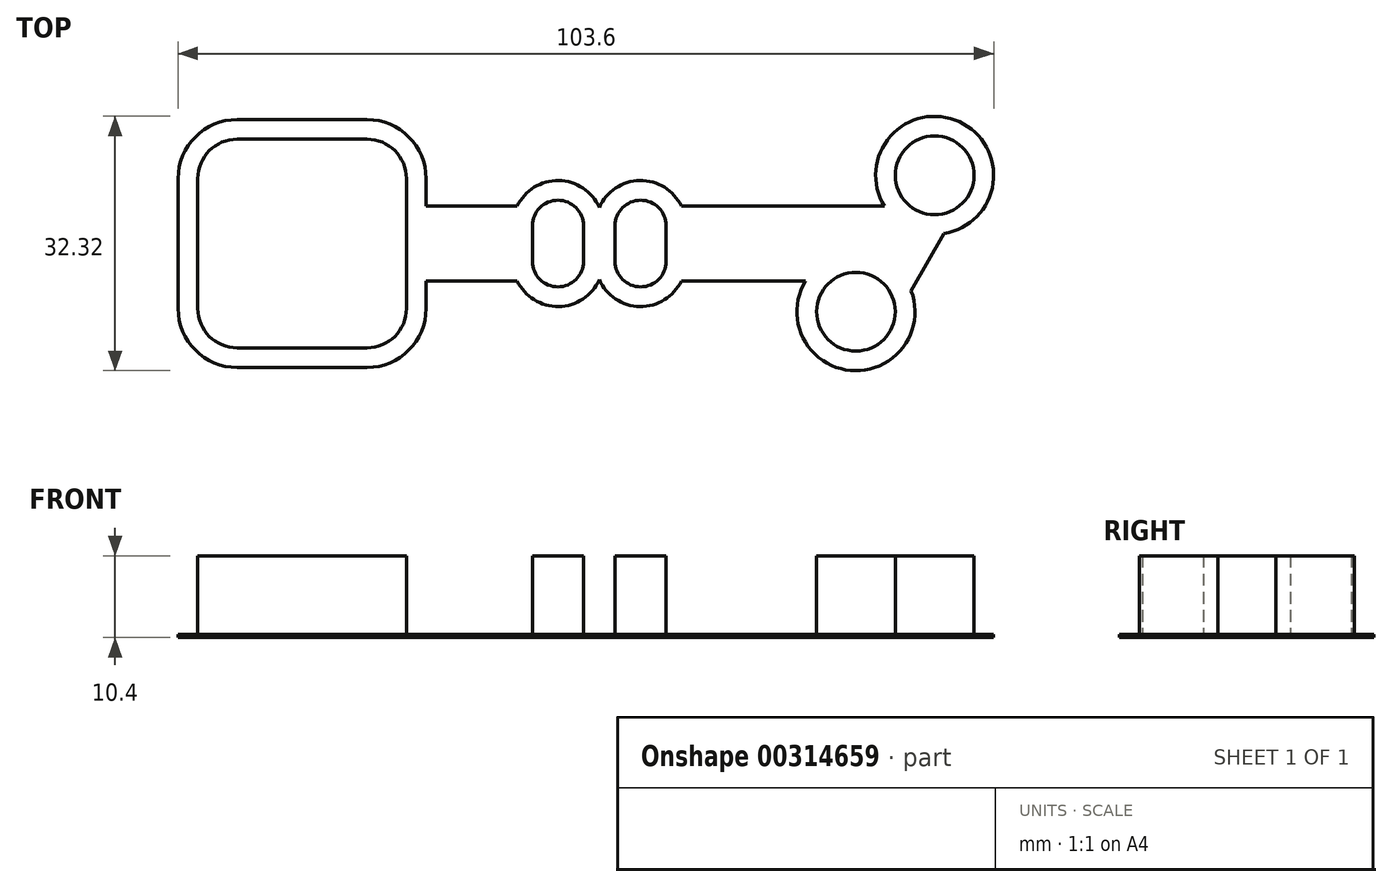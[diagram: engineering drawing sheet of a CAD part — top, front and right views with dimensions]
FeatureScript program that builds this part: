
annotation { "Feature Type Name" : "Feature", "Feature Type Description" : "" }
export const myFeature = defineFeature(function(context is Context, id is Id, definition is map)
    precondition{}
    {
        {
            var Q0;
            Q0=qCreatedBy(makeId("Top.planeOp"),FACE);
            var sketch = newSketch(context, id + "F0", { "sketchPlane" : qUnion([Q0])});
            skLineSegment(sketch, "E0.bottom", {"start": v(-8.25, 13.25) * mm, "end": v(8.25, 13.25) * mm});
            skLineSegment(sketch, "E0.top", {"start": v(-8.25, -13.25) * mm, "end": v(8.25, -13.25) * mm});
            skLineSegment(sketch, "E0.left", {"start": v(-13.25, 8.25) * mm, "end": v(-13.25, -8.25) * mm});
            skLineSegment(sketch, "E0.right", {"start": v(13.25, 8.25) * mm, "end": v(13.25, 2.25) * mm});
            skPoint(sketch, "E0.middle", {"position": v(0, 0) * mm});
            skPoint(sketch, "E1.visualSharp", {"position": v(-13.25, 13.25) * mm});
            skArc(sketch, "E1.filletArc", {"start": v(-8.25, 13.25) * mm, "mid": v(-11.79, 11.79) * mm, "end": v(-13.25, 8.25) * mm});
            skPoint(sketch, "E2.visualSharp", {"position": v(13.25, 13.25) * mm});
            skArc(sketch, "E2.filletArc", {"start": v(13.25, 8.25) * mm, "mid": v(11.79, 11.79) * mm, "end": v(8.25, 13.25) * mm});
            skPoint(sketch, "E3.visualSharp", {"position": v(13.25, -13.25) * mm});
            skArc(sketch, "E3.filletArc", {"start": v(8.25, -13.25) * mm, "mid": v(11.79, -11.79) * mm, "end": v(13.25, -8.25) * mm});
            skPoint(sketch, "E4.visualSharp", {"position": v(-13.25, -13.25) * mm});
            skArc(sketch, "E4.filletArc", {"start": v(-13.25, -8.25) * mm, "mid": v(-11.79, -11.79) * mm, "end": v(-8.25, -13.25) * mm});
            skCircle(sketch, "E5", {"center": v(0, 0) * mm, "radius": 4.5 * mm});
            skLineSegment(sketch, "E6", {"start": v(-4.5, 13.25) * mm, "end": v(-4.5, -13.25) * mm});
            skLineSegment(sketch, "E7", {"start": v(4.5, 13.25) * mm, "end": v(4.5, -13.25) * mm});
            skLineSegment(sketch, "E8", {"start": v(-13.25, 4.5) * mm, "end": v(13.25, 4.5) * mm});
            skLineSegment(sketch, "E9", {"start": v(-13.25, -4.5) * mm, "end": v(13.25, -4.5) * mm});
            skLineSegment(sketch, "E10", {"start": v(-29.26, 0) * mm, "end": v(84.97, 0) * mm, "construction": true});
            skPoint(sketch, "E10.startSnap0", {"position": v(-4.5, 0) * mm});
            skPoint(sketch, "E10.endSnap0", {"position": v(13.25, 0) * mm});
            skLineSegment(sketch, "E11", {"start": v(13.25, 2.25) * mm, "end": v(29.25, 2.25) * mm});
            skLineSegment(sketch, "E12.bottom", {"start": v(29.25, 2.25) * mm, "end": v(35.75, 2.25) * mm});
            skLineSegment(sketch, "E12.top", {"start": v(29.25, -2.25) * mm, "end": v(35.75, -2.25) * mm});
            skLineSegment(sketch, "E12.left", {"start": v(29.25, 2.25) * mm, "end": v(29.25, -2.25) * mm});
            skLineSegment(sketch, "E12.right", {"start": v(35.75, 2.25) * mm, "end": v(35.75, -2.25) * mm});
            skLineSegment(sketch, "E13", {"start": v(37.75, 11.92) * mm, "end": v(37.75, -12.1) * mm, "construction": true});
            skLineSegment(sketch, "E14.MirrorCS", {"start": v(13.25, -2.25) * mm, "end": v(29.25, -2.25) * mm});
            skLineSegment(sketch, "E15.MirrorCS", {"start": v(46.25, 2.25) * mm, "end": v(39.75, 2.25) * mm});
            skLineSegment(sketch, "E16.MirrorCS", {"start": v(39.75, 2.25) * mm, "end": v(39.75, -2.25) * mm});
            skLineSegment(sketch, "E17.MirrorCS", {"start": v(46.25, -2.25) * mm, "end": v(39.75, -2.25) * mm});
            skLineSegment(sketch, "E18.MirrorCS", {"start": v(46.25, 2.25) * mm, "end": v(46.25, -2.25) * mm});
            skLineSegment(sketch, "E19", {"start": v(35.75, -2.25) * mm, "end": v(39.75, -2.25) * mm});
            skLineSegment(sketch, "E20", {"start": v(35.75, 2.25) * mm, "end": v(39.75, 2.25) * mm});
            skArc(sketch, "E21", {"start": v(29.25, 2.25) * mm, "mid": v(32.5, 5.5) * mm, "end": v(35.75, 2.25) * mm});
            skArc(sketch, "E22", {"start": v(29.25, -2.25) * mm, "mid": v(32.5, -5.5) * mm, "end": v(35.75, -2.25) * mm});
            skArc(sketch, "E23.MirrorCS", {"start": v(46.25, 2.25) * mm, "mid": v(43, 5.5) * mm, "end": v(39.75, 2.25) * mm});
            skArc(sketch, "E24.MirrorCS", {"start": v(46.25, -2.25) * mm, "mid": v(43, -5.5) * mm, "end": v(39.75, -2.25) * mm});
            skLineSegment(sketch, "E25", {"start": v(46.25, 2.25) * mm, "end": v(74.05, 2.25) * mm});
            skLineSegment(sketch, "E26", {"start": v(70.35, -8.66) * mm, "end": v(80.35, 8.66) * mm, "construction": true});
            skPoint(sketch, "E27", {"position": v(75.35, 0) * mm});
            skLineSegment(sketch, "E28", {"start": v(76.17, 5.92) * mm, "end": v(74.05, 2.25) * mm});
            skLineSegment(sketch, "E29.MirrorCS", {"start": v(80.06, 3.67) * mm, "end": v(80.06, 3.67) * mm});
            skPoint(sketch, "E30", {"position": v(72.75, 0) * mm});
            skLineSegment(sketch, "E31.MirrorCS", {"start": v(46.25, -2.25) * mm, "end": v(71.45, -2.25) * mm});
            skPoint(sketch, "E32.orphan", {"position": v(72.75, -2.25) * mm});
            skPoint(sketch, "E33.orphan", {"position": v(72.75, 2.25) * mm});
            skLineSegment(sketch, "E34", {"start": v(13.25, 2.25) * mm, "end": v(13.25, 2.25) * mm});
            skArc(sketch, "E35", {"start": v(74.53, -5.92) * mm, "mid": v(72.85, -4.33) * mm, "end": v(70.63, -3.67) * mm});
            skArc(sketch, "E36", {"start": v(70.63, -3.67) * mm, "mid": v(67.85, -13) * mm, "end": v(74.53, -5.92) * mm});
            skLineSegment(sketch, "E37", {"start": v(80.06, 3.67) * mm, "end": v(74.53, -5.92) * mm});
            skArc(sketch, "E38", {"start": v(76.17, 5.92) * mm, "mid": v(77.85, 4.33) * mm, "end": v(80.06, 3.67) * mm});
            skArc(sketch, "E39", {"start": v(80.06, 3.67) * mm, "mid": v(82.85, 13) * mm, "end": v(76.17, 5.92) * mm});
            skLineSegment(sketch, "E40", {"start": v(13.25, -2.25) * mm, "end": v(13.25, -2.25) * mm});
            skLineSegment(sketch, "E41", {"start": v(13.25, -2.25) * mm, "end": v(13.25, -8.25) * mm});
            skLineSegment(sketch, "E42", {"start": v(13.25, 2.25) * mm, "end": v(13.25, -2.25) * mm});
            skLineSegment(sketch, "E43", {"start": v(71.45, -2.25) * mm, "end": v(70.63, -3.67) * mm});
            skLineSegment(sketch, "E44", {"start": v(74.05, 2.25) * mm, "end": v(71.45, -2.25) * mm});
            skLineSegment(sketch, "E45.0", {"start": v(81.56, 1.26) * mm, "end": v(77.36, -6) * mm});
            skArc(sketch, "E45.1", {"start": v(63.95, -4.75) * mm, "mid": v(69.65, -16.13) * mm, "end": v(77.36, -6) * mm});
            skLineSegment(sketch, "E45.2", {"start": v(48.18, -4.75) * mm, "end": v(63.95, -4.75) * mm});
            skArc(sketch, "E45.3", {"start": v(48.18, -4.75) * mm, "mid": v(42.91, -8) * mm, "end": v(37.75, -4.6) * mm});
            skArc(sketch, "E45.4", {"start": v(27.32, -4.75) * mm, "mid": v(32.59, -8) * mm, "end": v(37.75, -4.6) * mm});
            skArc(sketch, "E45.5", {"start": v(81.56, 1.26) * mm, "mid": v(83.47, 15.48) * mm, "end": v(73.95, 4.75) * mm});
            skLineSegment(sketch, "E45.6", {"start": v(15.75, -4.75) * mm, "end": v(27.32, -4.75) * mm});
            skLineSegment(sketch, "E45.7", {"start": v(15.75, -4.75) * mm, "end": v(15.75, -8.25) * mm});
            skArc(sketch, "E45.8", {"start": v(8.25, -15.75) * mm, "mid": v(13.55, -13.55) * mm, "end": v(15.75, -8.25) * mm});
            skLineSegment(sketch, "E45.9", {"start": v(-8.25, -15.75) * mm, "end": v(8.25, -15.75) * mm});
            skLineSegment(sketch, "E45.10", {"start": v(15.75, 4.75) * mm, "end": v(27.32, 4.75) * mm});
            skArc(sketch, "E45.11", {"start": v(27.32, 4.75) * mm, "mid": v(32.59, 8) * mm, "end": v(37.75, 4.6) * mm});
            skArc(sketch, "E45.12", {"start": v(48.18, 4.75) * mm, "mid": v(42.91, 8) * mm, "end": v(37.75, 4.6) * mm});
            skLineSegment(sketch, "E45.13", {"start": v(48.18, 4.75) * mm, "end": v(73.95, 4.75) * mm});
            skLineSegment(sketch, "E45.14", {"start": v(15.75, 8.25) * mm, "end": v(15.75, 4.75) * mm});
            skArc(sketch, "E45.15", {"start": v(15.75, 8.25) * mm, "mid": v(13.55, 13.55) * mm, "end": v(8.25, 15.75) * mm});
            skLineSegment(sketch, "E45.16", {"start": v(-8.25, 15.75) * mm, "end": v(8.25, 15.75) * mm});
            skArc(sketch, "E45.17", {"start": v(-8.25, 15.75) * mm, "mid": v(-13.55, 13.55) * mm, "end": v(-15.75, 8.25) * mm});
            skLineSegment(sketch, "E45.18", {"start": v(-15.75, 8.25) * mm, "end": v(-15.75, -8.25) * mm});
            skArc(sketch, "E45.19", {"start": v(-15.75, -8.25) * mm, "mid": v(-13.55, -13.55) * mm, "end": v(-8.25, -15.75) * mm});
            skSolve(sketch);
        }
        {
            var Q0;
            Q0=makeQuery(id+"F0.imprint","IMPRINT",FACE,{"disambiguationData":[TD([[makeQuery(id+"F0.imprint","IMPRINT",EDGE,{"derivedFrom":sQuery(id+"F0.wireOp",EDGE,"E12.right")}),1.0]])]});
            var Q1;
            {var subQ0=sQuery(id+"F0.wireOp",EDGE,"E7");var subQ1=sQuery(id+"F0.wireOp",EDGE,"E5");var subQ2=makeQuery(id+"F0.imprint","INTERSECT",VERTEX,{"derivedFrom":[subQ1,subQ0]});Q1=makeQuery(id+"F0.imprint","IMPRINT",FACE,{"disambiguationData":[TD([[makeQuery(id+"F0.imprint","IMPRINT",EDGE,{"disambiguationData":[TD([[subQ2,1.0]])],"derivedFrom":subQ1}),-1.0]])]});}
            var Q2;
            {var subQ5=sQuery(id+"F0.wireOp",EDGE,"E4.filletArc");Q2=makeQuery(id+"F0.imprint","IMPRINT",FACE,{"disambiguationData":[TD([[makeQuery(id+"F0.imprint","IMPRINT",EDGE,{"derivedFrom":subQ5}),1.0]])]});}
            var Q3;
            {var subQ1=sQuery(id+"F0.wireOp",EDGE,"E0.top");var subQ5=sQuery(id+"F0.wireOp",EDGE,"E6");var subQ6=makeQuery(id+"F0.imprint","INTERSECT",VERTEX,{"derivedFrom":[subQ1,subQ5]});Q3=makeQuery(id+"F0.imprint","IMPRINT",FACE,{"disambiguationData":[TD([[makeQuery(id+"F0.imprint","IMPRINT",EDGE,{"disambiguationData":[TD([[subQ6,-1.0]])],"derivedFrom":subQ1}),1.0]])]});}
            var Q4;
            Q4=makeQuery(id+"F0.imprint","IMPRINT",FACE,{"disambiguationData":[TD([[makeQuery(id+"F0.imprint","IMPRINT",EDGE,{"derivedFrom":sQuery(id+"F0.wireOp",EDGE,"E11")}),-1.0]])]});
            var Q5;
            Q5=makeQuery(id+"F0.imprint","IMPRINT",FACE,{"disambiguationData":[TD([[makeQuery(id+"F0.imprint","IMPRINT",EDGE,{"derivedFrom":sQuery(id+"F0.wireOp",EDGE,"E18.MirrorCS")}),1.0]])]});
            var Q6;
            Q6=makeQuery(id+"F0.imprint","IMPRINT",FACE,{"disambiguationData":[TD([[makeQuery(id+"F0.imprint","IMPRINT",EDGE,{"derivedFrom":sQuery(id+"F0.wireOp",EDGE,"E12.bottom")}),-1.0]])]});
            var Q7;
            Q7=makeQuery(id+"F0.imprint","IMPRINT",FACE,{"disambiguationData":[TD([[makeQuery(id+"F0.imprint","IMPRINT",EDGE,{"derivedFrom":sQuery(id+"F0.wireOp",EDGE,"E35")}),1.0]])]});
            var Q8;
            {var subQ8=sQuery(id+"F0.wireOp",EDGE,"E42");Q8=makeQuery(id+"F0.imprint","IMPRINT",FACE,{"disambiguationData":[TD([[makeQuery(id+"F0.imprint","IMPRINT",EDGE,{"derivedFrom":subQ8}),-1.0]])]});}
            var Q9;
            {var subQ4=sQuery(id+"F0.wireOp",EDGE,"E8");var subQ6=sQuery(id+"F0.wireOp",EDGE,"E0.left");var subQ8=makeQuery(id+"F0.imprint","INTERSECT",VERTEX,{"derivedFrom":[subQ6,subQ4]});Q9=makeQuery(id+"F0.imprint","IMPRINT",FACE,{"disambiguationData":[TD([[makeQuery(id+"F0.imprint","IMPRINT",EDGE,{"disambiguationData":[TD([[subQ8,-1.0]])],"derivedFrom":subQ6}),1.0]])]});}
            var Q10;
            {var subQ0=sQuery(id+"F0.wireOp",EDGE,"E5");var subQ1=makeQuery(id+"F0.imprint","INTERSECT",VERTEX,{"derivedFrom":[subQ0,sQuery(id+"F0.wireOp",EDGE,"E8")]});Q10=makeQuery(id+"F0.imprint","IMPRINT",FACE,{"disambiguationData":[TD([[makeQuery(id+"F0.imprint","IMPRINT",EDGE,{"disambiguationData":[TD([[subQ1,1.0]])],"derivedFrom":subQ0}),1.0]])]});}
            var Q11;
            {var subQ9=sQuery(id+"F0.wireOp",EDGE,"E1.filletArc");Q11=makeQuery(id+"F0.imprint","IMPRINT",FACE,{"disambiguationData":[TD([[makeQuery(id+"F0.imprint","IMPRINT",EDGE,{"derivedFrom":subQ9}),-1.0]])]});}
            var Q12;
            Q12=makeQuery(id+"F0.imprint","IMPRINT",FACE,{"disambiguationData":[TD([[makeQuery(id+"F0.imprint","IMPRINT",EDGE,{"derivedFrom":sQuery(id+"F0.wireOp",EDGE,"E38")}),1.0]])]});
            var Q13;
            {var subQ5=sQuery(id+"F0.wireOp",EDGE,"E2.filletArc");Q13=makeQuery(id+"F0.imprint","IMPRINT",FACE,{"disambiguationData":[TD([[makeQuery(id+"F0.imprint","IMPRINT",EDGE,{"derivedFrom":subQ5}),1.0]])]});}
            var Q14;
            {var subQ5=sQuery(id+"F0.wireOp",EDGE,"E1.filletArc");Q14=makeQuery(id+"F0.imprint","IMPRINT",FACE,{"disambiguationData":[TD([[makeQuery(id+"F0.imprint","IMPRINT",EDGE,{"derivedFrom":subQ5}),1.0]])]});}
            var Q15;
            {var subQ0=sQuery(id+"F0.wireOp",EDGE,"E8");var subQ1=sQuery(id+"F0.wireOp",EDGE,"E5");var subQ2=makeQuery(id+"F0.imprint","INTERSECT",VERTEX,{"derivedFrom":[subQ1,subQ0]});Q15=makeQuery(id+"F0.imprint","IMPRINT",FACE,{"disambiguationData":[TD([[makeQuery(id+"F0.imprint","IMPRINT",EDGE,{"disambiguationData":[TD([[subQ2,1.0]])],"derivedFrom":subQ1}),-1.0]])]});}
            var Q16;
            {var subQ0=sQuery(id+"F0.wireOp",EDGE,"E6");var subQ1=sQuery(id+"F0.wireOp",EDGE,"E5");var subQ2=makeQuery(id+"F0.imprint","INTERSECT",VERTEX,{"derivedFrom":[subQ1,subQ0]});Q16=makeQuery(id+"F0.imprint","IMPRINT",FACE,{"disambiguationData":[TD([[makeQuery(id+"F0.imprint","IMPRINT",EDGE,{"disambiguationData":[TD([[subQ2,-1.0]])],"derivedFrom":subQ1}),-1.0]])]});}
            var Q17;
            {var subQ0=sQuery(id+"F0.wireOp",EDGE,"E8");var subQ1=sQuery(id+"F0.wireOp",EDGE,"E5");var subQ2=makeQuery(id+"F0.imprint","INTERSECT",VERTEX,{"derivedFrom":[subQ1,subQ0]});Q17=makeQuery(id+"F0.imprint","IMPRINT",FACE,{"disambiguationData":[TD([[makeQuery(id+"F0.imprint","IMPRINT",EDGE,{"disambiguationData":[TD([[subQ2,-1.0]])],"derivedFrom":subQ1}),-1.0]])]});}
            var Q18;
            {var subQ7=sQuery(id+"F0.wireOp",EDGE,"E3.filletArc");Q18=makeQuery(id+"F0.imprint","IMPRINT",FACE,{"disambiguationData":[TD([[makeQuery(id+"F0.imprint","IMPRINT",EDGE,{"derivedFrom":subQ7}),1.0]])]});}
            var Q19;
            Q19=makeQuery(id+"F0.imprint","IMPRINT",FACE,{"disambiguationData":[TD([[makeQuery(id+"F0.imprint","IMPRINT",EDGE,{"derivedFrom":sQuery(id+"F0.wireOp",EDGE,"E17.MirrorCS")}),1.0]])]});
            var Q20;
            Q20=makeQuery(id+"F0.imprint","IMPRINT",FACE,{"disambiguationData":[TD([[makeQuery(id+"F0.imprint","IMPRINT",EDGE,{"derivedFrom":sQuery(id+"F0.wireOp",EDGE,"E15.MirrorCS")}),-1.0]])]});
            var Q21;
            Q21=makeQuery(id+"F0.imprint","IMPRINT",FACE,{"disambiguationData":[TD([[makeQuery(id+"F0.imprint","IMPRINT",EDGE,{"derivedFrom":sQuery(id+"F0.wireOp",EDGE,"E12.top")}),-1.0]])]});
            var Q22;
            Q22=makeQuery(id+"F0.imprint","IMPRINT",FACE,{"disambiguationData":[TD([[makeQuery(id+"F0.imprint","IMPRINT",EDGE,{"derivedFrom":sQuery(id+"F0.wireOp",EDGE,"E12.bottom")}),1.0]])]});
            var Q23;
            {var subQ2=sQuery(id+"F0.wireOp",EDGE,"E6");var subQ5=sQuery(id+"F0.wireOp",EDGE,"E0.bottom");var subQ8=makeQuery(id+"F0.imprint","INTERSECT",VERTEX,{"derivedFrom":[subQ5,subQ2]});Q23=makeQuery(id+"F0.imprint","IMPRINT",FACE,{"disambiguationData":[TD([[makeQuery(id+"F0.imprint","IMPRINT",EDGE,{"disambiguationData":[TD([[subQ8,-1.0]])],"derivedFrom":subQ5}),-1.0]])]});}
            var Q24;
            Q24=makeQuery(id+"F0.imprint","IMPRINT",FACE,{"disambiguationData":[TD([[makeQuery(id+"F0.imprint","IMPRINT",EDGE,{"derivedFrom":sQuery(id+"F0.wireOp",EDGE,"E28")}),1.0]])]});
            var Q25;
            Q25=makeQuery(id+"F0.imprint","IMPRINT",FACE,{"disambiguationData":[TD([[makeQuery(id+"F0.imprint","IMPRINT",EDGE,{"derivedFrom":sQuery(id+"F0.wireOp",EDGE,"E15.MirrorCS")}),1.0]])]});
            extrude(context, id + "F1", {"entities" : qUnion([Q0, Q1, Q2, Q3, Q4, Q5, Q6, Q7, Q8, Q9, Q10, Q11, Q12, Q13, Q14, Q15, Q16, Q17, Q18, Q19, Q20, Q21, Q22, Q23, Q24, Q25]), "depth" : 0.4 * mm});
        }
        {
            var Q0;
            Q0=makeQuery(id+"F1.opExtrude","CAP_FACE",FACE,{"disambiguationData":[OSD([sQuery(id+"F0.wireOp",EDGE,"E45.0"),sQuery(id+"F0.wireOp",EDGE,"E45.1"),sQuery(id+"F0.wireOp",EDGE,"E45.2"),sQuery(id+"F0.wireOp",EDGE,"E45.3"),sQuery(id+"F0.wireOp",EDGE,"E45.4"),sQuery(id+"F0.wireOp",EDGE,"E45.5"),sQuery(id+"F0.wireOp",EDGE,"E45.6"),sQuery(id+"F0.wireOp",EDGE,"E45.7"),sQuery(id+"F0.wireOp",EDGE,"E45.8"),sQuery(id+"F0.wireOp",EDGE,"E45.9"),sQuery(id+"F0.wireOp",EDGE,"E45.10"),sQuery(id+"F0.wireOp",EDGE,"E45.11"),sQuery(id+"F0.wireOp",EDGE,"E45.12"),sQuery(id+"F0.wireOp",EDGE,"E45.13"),sQuery(id+"F0.wireOp",EDGE,"E45.14"),sQuery(id+"F0.wireOp",EDGE,"E45.15"),sQuery(id+"F0.wireOp",EDGE,"E45.16"),sQuery(id+"F0.wireOp",EDGE,"E45.17"),sQuery(id+"F0.wireOp",EDGE,"E45.18"),sQuery(id+"F0.wireOp",EDGE,"E45.19")])],"isStart":false});
            var sketch = newSketch(context, id + "F2", { "sketchPlane" : qUnion([Q0])});
            skLineSegment(sketch, "E46.0.0", {"start": v(8.25, 15.75) * mm, "end": v(-8.25, 15.75) * mm});
            skArc(sketch, "E46.0.1", {"start": v(-8.25, 15.75) * mm, "mid": v(-13.55, 13.55) * mm, "end": v(-15.75, 8.25) * mm});
            skLineSegment(sketch, "E46.0.2", {"start": v(-15.75, 8.25) * mm, "end": v(-15.75, -8.25) * mm});
            skArc(sketch, "E46.0.3", {"start": v(-15.75, -8.25) * mm, "mid": v(-13.55, -13.55) * mm, "end": v(-8.25, -15.75) * mm});
            skLineSegment(sketch, "E46.0.4", {"start": v(-8.25, -15.75) * mm, "end": v(8.25, -15.75) * mm});
            skArc(sketch, "E46.0.5", {"start": v(8.25, -15.75) * mm, "mid": v(13.55, -13.55) * mm, "end": v(15.75, -8.25) * mm});
            skLineSegment(sketch, "E46.0.6", {"start": v(15.75, -8.25) * mm, "end": v(15.75, -4.75) * mm});
            skLineSegment(sketch, "E46.0.7", {"start": v(15.75, -4.75) * mm, "end": v(27.32, -4.75) * mm});
            skArc(sketch, "E46.0.8", {"start": v(27.32, -4.75) * mm, "mid": v(32.59, -8) * mm, "end": v(37.75, -4.6) * mm});
            skArc(sketch, "E46.0.9", {"start": v(37.75, -4.6) * mm, "mid": v(42.91, -8) * mm, "end": v(48.18, -4.75) * mm});
            skLineSegment(sketch, "E46.0.10", {"start": v(48.18, -4.75) * mm, "end": v(63.95, -4.75) * mm});
            skArc(sketch, "E46.0.11", {"start": v(63.95, -4.75) * mm, "mid": v(69.65, -16.13) * mm, "end": v(77.36, -6) * mm});
            skLineSegment(sketch, "E46.0.12", {"start": v(77.36, -6) * mm, "end": v(81.56, 1.26) * mm});
            skArc(sketch, "E46.0.13", {"start": v(81.56, 1.26) * mm, "mid": v(83.47, 15.48) * mm, "end": v(73.95, 4.75) * mm});
            skLineSegment(sketch, "E46.0.14", {"start": v(73.95, 4.75) * mm, "end": v(48.18, 4.75) * mm});
            skArc(sketch, "E46.0.15", {"start": v(48.18, 4.75) * mm, "mid": v(42.91, 8) * mm, "end": v(37.75, 4.6) * mm});
            skArc(sketch, "E46.0.16", {"start": v(37.75, 4.6) * mm, "mid": v(32.59, 8) * mm, "end": v(27.32, 4.75) * mm});
            skLineSegment(sketch, "E46.0.17", {"start": v(27.32, 4.75) * mm, "end": v(15.75, 4.75) * mm});
            skLineSegment(sketch, "E46.0.18", {"start": v(15.75, 4.75) * mm, "end": v(15.75, 8.25) * mm});
            skArc(sketch, "E46.0.19", {"start": v(15.75, 8.25) * mm, "mid": v(13.55, 13.55) * mm, "end": v(8.25, 15.75) * mm});
            skLineSegment(sketch, "E47.0", {"start": v(-8.25, 13.25) * mm, "end": v(8.25, 13.25) * mm});
            skLineSegment(sketch, "E47.1", {"start": v(-8.25, -13.25) * mm, "end": v(8.25, -13.25) * mm});
            skLineSegment(sketch, "E47.2", {"start": v(-13.25, 8.25) * mm, "end": v(-13.25, -8.25) * mm});
            skLineSegment(sketch, "E47.3", {"start": v(13.25, 8.25) * mm, "end": v(13.25, 2.25) * mm});
            skPoint(sketch, "E47.4", {"position": v(0, 0) * mm});
            skPoint(sketch, "E47.5", {"position": v(-13.25, 13.25) * mm});
            skArc(sketch, "E47.6", {"start": v(-8.25, 13.25) * mm, "mid": v(-11.79, 11.79) * mm, "end": v(-13.25, 8.25) * mm});
            skPoint(sketch, "E47.7", {"position": v(13.25, 13.25) * mm});
            skArc(sketch, "E47.8", {"start": v(13.25, 8.25) * mm, "mid": v(11.79, 11.79) * mm, "end": v(8.25, 13.25) * mm});
            skPoint(sketch, "E47.9", {"position": v(13.25, -13.25) * mm});
            skArc(sketch, "E47.10", {"start": v(8.25, -13.25) * mm, "mid": v(11.79, -11.79) * mm, "end": v(13.25, -8.25) * mm});
            skPoint(sketch, "E47.11", {"position": v(-13.25, -13.25) * mm});
            skArc(sketch, "E47.12", {"start": v(-13.25, -8.25) * mm, "mid": v(-11.79, -11.79) * mm, "end": v(-8.25, -13.25) * mm});
            skCircle(sketch, "E47.13", {"center": v(0, 0) * mm, "radius": 4.5 * mm});
            skLineSegment(sketch, "E47.14", {"start": v(-4.5, 13.25) * mm, "end": v(-4.5, -13.25) * mm});
            skLineSegment(sketch, "E47.15", {"start": v(4.5, 13.25) * mm, "end": v(4.5, -13.25) * mm});
            skLineSegment(sketch, "E47.16", {"start": v(-13.25, 4.5) * mm, "end": v(13.25, 4.5) * mm});
            skLineSegment(sketch, "E47.17", {"start": v(-13.25, -4.5) * mm, "end": v(13.25, -4.5) * mm});
            skPoint(sketch, "E47.19", {"position": v(-4.5, 0) * mm});
            skPoint(sketch, "E47.20", {"position": v(13.25, 0) * mm});
            skLineSegment(sketch, "E47.21", {"start": v(13.25, 2.25) * mm, "end": v(29.25, 2.25) * mm});
            skLineSegment(sketch, "E47.22", {"start": v(29.25, 2.25) * mm, "end": v(35.75, 2.25) * mm});
            skLineSegment(sketch, "E47.23", {"start": v(29.25, -2.25) * mm, "end": v(35.75, -2.25) * mm});
            skLineSegment(sketch, "E47.24", {"start": v(29.25, 2.25) * mm, "end": v(29.25, -2.25) * mm});
            skLineSegment(sketch, "E47.25", {"start": v(35.75, 2.25) * mm, "end": v(35.75, -2.25) * mm});
            skLineSegment(sketch, "E47.27", {"start": v(13.25, -2.25) * mm, "end": v(29.25, -2.25) * mm});
            skLineSegment(sketch, "E47.28", {"start": v(46.25, 2.25) * mm, "end": v(39.75, 2.25) * mm});
            skLineSegment(sketch, "E47.29", {"start": v(39.75, 2.25) * mm, "end": v(39.75, -2.25) * mm});
            skLineSegment(sketch, "E47.30", {"start": v(46.25, -2.25) * mm, "end": v(39.75, -2.25) * mm});
            skLineSegment(sketch, "E47.31", {"start": v(46.25, 2.25) * mm, "end": v(46.25, -2.25) * mm});
            skLineSegment(sketch, "E47.32", {"start": v(35.75, -2.25) * mm, "end": v(39.75, -2.25) * mm});
            skLineSegment(sketch, "E47.33", {"start": v(35.75, 2.25) * mm, "end": v(39.75, 2.25) * mm});
            skArc(sketch, "E47.34", {"start": v(29.25, 2.25) * mm, "mid": v(32.5, 5.5) * mm, "end": v(35.75, 2.25) * mm});
            skArc(sketch, "E47.35", {"start": v(29.25, -2.25) * mm, "mid": v(32.5, -5.5) * mm, "end": v(35.75, -2.25) * mm});
            skArc(sketch, "E47.36", {"start": v(46.25, 2.25) * mm, "mid": v(43, 5.5) * mm, "end": v(39.75, 2.25) * mm});
            skArc(sketch, "E47.37", {"start": v(46.25, -2.25) * mm, "mid": v(43, -5.5) * mm, "end": v(39.75, -2.25) * mm});
            skLineSegment(sketch, "E47.38", {"start": v(46.25, 2.25) * mm, "end": v(74.05, 2.25) * mm});
            skLineSegment(sketch, "E47.39", {"start": v(70.35, -8.66) * mm, "end": v(80.35, 8.66) * mm});
            skPoint(sketch, "E47.40", {"position": v(75.35, 0) * mm});
            skLineSegment(sketch, "E47.41", {"start": v(76.17, 5.92) * mm, "end": v(74.05, 2.25) * mm});
            skPoint(sketch, "E47.42", {"position": v(80.06, 3.67) * mm});
            skPoint(sketch, "E47.43", {"position": v(72.75, 0) * mm});
            skLineSegment(sketch, "E47.44", {"start": v(46.25, -2.25) * mm, "end": v(71.45, -2.25) * mm});
            skPoint(sketch, "E47.47", {"position": v(13.25, 2.25) * mm});
            skArc(sketch, "E47.48", {"start": v(74.53, -5.92) * mm, "mid": v(72.85, -4.33) * mm, "end": v(70.63, -3.67) * mm});
            skArc(sketch, "E47.49", {"start": v(70.63, -3.67) * mm, "mid": v(67.85, -13) * mm, "end": v(74.53, -5.92) * mm});
            skLineSegment(sketch, "E47.50", {"start": v(80.06, 3.67) * mm, "end": v(74.53, -5.92) * mm});
            skArc(sketch, "E47.51", {"start": v(76.17, 5.92) * mm, "mid": v(77.85, 4.33) * mm, "end": v(80.06, 3.67) * mm});
            skArc(sketch, "E47.52", {"start": v(80.06, 3.67) * mm, "mid": v(82.85, 13) * mm, "end": v(76.17, 5.92) * mm});
            skPoint(sketch, "E47.53", {"position": v(13.25, -2.25) * mm});
            skLineSegment(sketch, "E47.54", {"start": v(13.25, -2.25) * mm, "end": v(13.25, -8.25) * mm});
            skLineSegment(sketch, "E47.55", {"start": v(13.25, 2.25) * mm, "end": v(13.25, -2.25) * mm});
            skLineSegment(sketch, "E47.56", {"start": v(71.45, -2.25) * mm, "end": v(70.63, -3.67) * mm});
            skLineSegment(sketch, "E47.57", {"start": v(74.05, 2.25) * mm, "end": v(71.45, -2.25) * mm});
            skLineSegment(sketch, "E47.58", {"start": v(81.56, 1.26) * mm, "end": v(77.36, -6) * mm});
            skArc(sketch, "E47.61", {"start": v(48.18, -4.75) * mm, "mid": v(42.91, -8) * mm, "end": v(37.75, -4.6) * mm});
            skLineSegment(sketch, "E47.65", {"start": v(15.75, -4.75) * mm, "end": v(15.75, -8.25) * mm});
            skLineSegment(sketch, "E47.68", {"start": v(15.75, 4.75) * mm, "end": v(27.32, 4.75) * mm});
            skArc(sketch, "E47.69", {"start": v(27.32, 4.75) * mm, "mid": v(32.59, 8) * mm, "end": v(37.75, 4.6) * mm});
            skLineSegment(sketch, "E47.71", {"start": v(48.18, 4.75) * mm, "end": v(73.95, 4.75) * mm});
            skLineSegment(sketch, "E47.72", {"start": v(15.75, 8.25) * mm, "end": v(15.75, 4.75) * mm});
            skLineSegment(sketch, "E47.74", {"start": v(-8.25, 15.75) * mm, "end": v(8.25, 15.75) * mm});
            skSolve(sketch);
        }
        {
            var Q0;
            {var subQ5=sQuery(id+"F2.wireOp",EDGE,"E47.8");Q0=makeQuery(id+"F2.imprint","IMPRINT",FACE,{"disambiguationData":[TD([[makeQuery(id+"F2.imprint","IMPRINT",EDGE,{"derivedFrom":subQ5}),1.0]])]});}
            var Q1;
            {var subQ2=sQuery(id+"F2.wireOp",EDGE,"E47.14");var subQ5=sQuery(id+"F2.wireOp",EDGE,"E47.0");var subQ8=makeQuery(id+"F2.imprint","INTERSECT",VERTEX,{"derivedFrom":[subQ5,subQ2]});Q1=makeQuery(id+"F2.imprint","IMPRINT",FACE,{"disambiguationData":[TD([[makeQuery(id+"F2.imprint","IMPRINT",EDGE,{"disambiguationData":[TD([[subQ8,-1.0]])],"derivedFrom":subQ5}),-1.0]])]});}
            var Q2;
            {var subQ5=sQuery(id+"F2.wireOp",EDGE,"E47.6");Q2=makeQuery(id+"F2.imprint","IMPRINT",FACE,{"disambiguationData":[TD([[makeQuery(id+"F2.imprint","IMPRINT",EDGE,{"derivedFrom":subQ5}),1.0]])]});}
            var Q3;
            {var subQ4=sQuery(id+"F2.wireOp",EDGE,"E47.16");var subQ6=sQuery(id+"F2.wireOp",EDGE,"E47.2");var subQ8=makeQuery(id+"F2.imprint","INTERSECT",VERTEX,{"derivedFrom":[subQ6,subQ4]});Q3=makeQuery(id+"F2.imprint","IMPRINT",FACE,{"disambiguationData":[TD([[makeQuery(id+"F2.imprint","IMPRINT",EDGE,{"disambiguationData":[TD([[subQ8,-1.0]])],"derivedFrom":subQ6}),1.0]])]});}
            var Q4;
            {var subQ5=sQuery(id+"F2.wireOp",EDGE,"E47.12");Q4=makeQuery(id+"F2.imprint","IMPRINT",FACE,{"disambiguationData":[TD([[makeQuery(id+"F2.imprint","IMPRINT",EDGE,{"derivedFrom":subQ5}),1.0]])]});}
            var Q5;
            {var subQ7=sQuery(id+"F2.wireOp",EDGE,"E47.10");Q5=makeQuery(id+"F2.imprint","IMPRINT",FACE,{"disambiguationData":[TD([[makeQuery(id+"F2.imprint","IMPRINT",EDGE,{"derivedFrom":subQ7}),1.0]])]});}
            var Q6;
            {var subQ8=sQuery(id+"F2.wireOp",EDGE,"E47.55");Q6=makeQuery(id+"F2.imprint","IMPRINT",FACE,{"disambiguationData":[TD([[makeQuery(id+"F2.imprint","IMPRINT",EDGE,{"derivedFrom":subQ8}),-1.0]])]});}
            var Q7;
            {var subQ0=sQuery(id+"F2.wireOp",EDGE,"E47.16");var subQ1=sQuery(id+"F2.wireOp",EDGE,"E47.13");var subQ2=makeQuery(id+"F2.imprint","INTERSECT",VERTEX,{"derivedFrom":[subQ1,subQ0]});Q7=makeQuery(id+"F2.imprint","IMPRINT",FACE,{"disambiguationData":[TD([[makeQuery(id+"F2.imprint","IMPRINT",EDGE,{"disambiguationData":[TD([[subQ2,1.0]])],"derivedFrom":subQ1}),-1.0]])]});}
            var Q8;
            {var subQ0=sQuery(id+"F2.wireOp",EDGE,"E47.13");var subQ1=makeQuery(id+"F2.imprint","INTERSECT",VERTEX,{"derivedFrom":[subQ0,sQuery(id+"F2.wireOp",EDGE,"E47.16")]});Q8=makeQuery(id+"F2.imprint","IMPRINT",FACE,{"disambiguationData":[TD([[makeQuery(id+"F2.imprint","IMPRINT",EDGE,{"disambiguationData":[TD([[subQ1,1.0]])],"derivedFrom":subQ0}),1.0]])]});}
            var Q9;
            {var subQ0=sQuery(id+"F2.wireOp",EDGE,"E47.15");var subQ1=sQuery(id+"F2.wireOp",EDGE,"E47.13");var subQ2=makeQuery(id+"F2.imprint","INTERSECT",VERTEX,{"derivedFrom":[subQ1,subQ0]});Q9=makeQuery(id+"F2.imprint","IMPRINT",FACE,{"disambiguationData":[TD([[makeQuery(id+"F2.imprint","IMPRINT",EDGE,{"disambiguationData":[TD([[subQ2,1.0]])],"derivedFrom":subQ1}),-1.0]])]});}
            var Q10;
            {var subQ0=sQuery(id+"F2.wireOp",EDGE,"E47.14");var subQ1=sQuery(id+"F2.wireOp",EDGE,"E47.13");var subQ2=makeQuery(id+"F2.imprint","INTERSECT",VERTEX,{"derivedFrom":[subQ1,subQ0]});Q10=makeQuery(id+"F2.imprint","IMPRINT",FACE,{"disambiguationData":[TD([[makeQuery(id+"F2.imprint","IMPRINT",EDGE,{"disambiguationData":[TD([[subQ2,-1.0]])],"derivedFrom":subQ1}),-1.0]])]});}
            var Q11;
            {var subQ0=sQuery(id+"F2.wireOp",EDGE,"E47.16");var subQ1=sQuery(id+"F2.wireOp",EDGE,"E47.13");var subQ2=makeQuery(id+"F2.imprint","INTERSECT",VERTEX,{"derivedFrom":[subQ1,subQ0]});Q11=makeQuery(id+"F2.imprint","IMPRINT",FACE,{"disambiguationData":[TD([[makeQuery(id+"F2.imprint","IMPRINT",EDGE,{"disambiguationData":[TD([[subQ2,-1.0]])],"derivedFrom":subQ1}),-1.0]])]});}
            var Q12;
            {var subQ1=sQuery(id+"F2.wireOp",EDGE,"E47.1");var subQ5=sQuery(id+"F2.wireOp",EDGE,"E47.14");var subQ6=makeQuery(id+"F2.imprint","INTERSECT",VERTEX,{"derivedFrom":[subQ1,subQ5]});Q12=makeQuery(id+"F2.imprint","IMPRINT",FACE,{"disambiguationData":[TD([[makeQuery(id+"F2.imprint","IMPRINT",EDGE,{"disambiguationData":[TD([[subQ6,-1.0]])],"derivedFrom":subQ1}),1.0]])]});}
            var Q13;
            Q13=makeQuery(id+"F2.imprint","IMPRINT",FACE,{"disambiguationData":[TD([[makeQuery(id+"F2.imprint","IMPRINT",EDGE,{"derivedFrom":sQuery(id+"F2.wireOp",EDGE,"E47.22")}),1.0]])]});
            var Q14;
            Q14=makeQuery(id+"F2.imprint","IMPRINT",FACE,{"disambiguationData":[TD([[makeQuery(id+"F2.imprint","IMPRINT",EDGE,{"derivedFrom":sQuery(id+"F2.wireOp",EDGE,"E47.22")}),-1.0]])]});
            var Q15;
            Q15=makeQuery(id+"F2.imprint","IMPRINT",FACE,{"disambiguationData":[TD([[makeQuery(id+"F2.imprint","IMPRINT",EDGE,{"derivedFrom":sQuery(id+"F2.wireOp",EDGE,"E47.23")}),-1.0]])]});
            var Q16;
            Q16=makeQuery(id+"F2.imprint","IMPRINT",FACE,{"disambiguationData":[TD([[makeQuery(id+"F2.imprint","IMPRINT",EDGE,{"derivedFrom":sQuery(id+"F2.wireOp",EDGE,"E47.30")}),1.0]])]});
            var Q17;
            Q17=makeQuery(id+"F2.imprint","IMPRINT",FACE,{"disambiguationData":[TD([[makeQuery(id+"F2.imprint","IMPRINT",EDGE,{"derivedFrom":sQuery(id+"F2.wireOp",EDGE,"E47.28")}),1.0]])]});
            var Q18;
            Q18=makeQuery(id+"F2.imprint","IMPRINT",FACE,{"disambiguationData":[TD([[makeQuery(id+"F2.imprint","IMPRINT",EDGE,{"derivedFrom":sQuery(id+"F2.wireOp",EDGE,"E47.28")}),-1.0]])]});
            var Q19;
            {var subQ0=sQuery(id+"F2.wireOp",EDGE,"E47.49");Q19=makeQuery(id+"F2.imprint","IMPRINT",FACE,{"disambiguationData":[TD([[makeQuery(id+"F2.imprint","IMPRINT",EDGE,{"derivedFrom":subQ0}),1.0]])]});}
            var Q20;
            {var subQ0=sQuery(id+"F2.wireOp",EDGE,"E47.52");Q20=makeQuery(id+"F2.imprint","IMPRINT",FACE,{"disambiguationData":[TD([[makeQuery(id+"F2.imprint","IMPRINT",EDGE,{"derivedFrom":subQ0}),1.0]])]});}
            extrude(context, id + "F3", {"entities" : qUnion([Q0, Q1, Q2, Q3, Q4, Q5, Q6, Q7, Q8, Q9, Q10, Q11, Q12, Q13, Q14, Q15, Q16, Q17, Q18, Q19, Q20]), "operationType" : NewBodyOperationType.ADD, "depth" : 10 * mm});
        }
    });
